# Revit family: Qmax 900
name_source: partatom
category: Plumbing Fixtures
revit_build: Autodesk Revit 2013 (Build: 20120221_2030(x64)
units: mm (PartAtom-declared; Revit-internal decimal feet)

## types (5) — shared parameters
700-900 Step Connector - Colour = Black
700-900 Step Connector - Dimensions = 860mm x 45mm x 1065mm (LxWxH)
700-900 Step Connector - Material = High Density Polyethylene
700-900 Step Connector - Model Description = High capacity slot drainage channel system
700-900 Step Connector - Product Code = 32883
700-900 Step Connector - Recyclable = Fully recyclable
700-900 Step Connector - Recycled Material Content = 0%
700-900 Step Connector - Weight = 3.7 kg
ACO Hydraulic Design Software = http://www.acodesign.co.uk
Assembly Code = D2040
Chamber Connector - Channel Colour = Black
Chamber Connector - Channel Material = Medium Density Polyethylene
Chamber Connector - Dimensions = Female End=800mm x 900mm x 1105mm, Male End=800mm x 900mm x 1055mm  (LxWXH)
Chamber Connector - Model Description = High capacity slot drainage channel system
Chamber Connector - Product Code = 32846
Chamber Connector - Recyclable = Fully recyclable
Chamber Connector - Recycled Material Content = Variable %
Chamber Connector - Weight = 25.1 kg
Channel C.S.A = 413471mm²
Channel Colour = Black
Channel Material = Medium Density Polyethylene
Channel Recyclable = Fully recyclable
Channel Recycled Material Content = Variable %
Closing End Cap - Colour = Black
Closing End Cap - Dimensions = 860mm x 16mm x 1065mm (LxWxH)
Closing End Cap - Model Description = High capacity slot drainage channel system
Closing End Cap - Product Code = 32845
Closing End Cap - Recyclable = Fully recyclable
Closing End Cap - Recycled Material Content = 0%
Closing End Cap - Weight = 9.8 kg
Concrete Surround Volume - Load Class A 15 - F 900 = 0.91 m³/m
Edge Rail Recyclable = Fully recyclable
Edge Rail Recycled Material Content = Between 40% - 90%
Fax = +44 (0)1462 815895
Hydraulic Performance = http://www.aco.co.uk
Installation - Concrete Grade = Refer to brochure
Installation - Reinforcement Details = Refer to brochure
Installation Guidelines = http://www.aco.co.uk
Length = 2000 mm  [stored 6.56168 ft]
Load Class = A 15 - F 900
Maintenance Guidelines = http://www.aco.co.uk
Manufacturer = ACO Technologies plc - ACO Water Management Division
Model = ACO Qmax 900
Model Description = High capacity slot drainage channel system
Price = POA - contact ACO
Product Brochure = http://www.aco.co.uk
Product Page URL = http://www.aco.co.uk
Product Standard = BS EN 1433:2002 CE  marked
Revision = 1
Seal Colour = Black
Seal Material = EPDM
Seal Recyclable = Fully recyclable
Seal Recycled Material Content = 0%
Telephone = +44 (0)1462 816666
URL = www.aco.co.uk
Width Overall = 860 mm
zero-valued in all types: Cost, SerialNumber, TagNumber

## per-type parameters (varying)
| type | Closing End Cap - Material | Coarse Origin | Depth Overall | Drainage Slot Intake Area | Drainage Slot Width | E1-QFlow-DuctileIron | E2-QGuard-DuctileIron | E3-QFlow-GalvSteel | E4-QGuard-GalvSteel | E5-QSlot-GalvSteel | Edge Rail Colour | Edge Rail Finish | Edge Rail Material | Endcap_Origin | Floor Opening Width | Invert Depth | Material | Product Code | Product Dimensions | Product Weight | Step Con Origin | Type Comments | V_CoarseE1 | V_Coarse_E5 |
| 32840 - Q-Flow Edge - D.I | High Density Polyethylene | 746 mm | 1270 mm | 18775mm²/m | 26mm | Yes | No | No | No | No | Black | ATec coating | Ductile Iron | 706 mm | 65 mm  [stored 0.213255 ft] | 1155mm | Iron, Ductile | 32840 | 2000mm x 860mm x 1270mm (LxWxH) | 65.3 kg | 681 mm  [stored 2.23425 ft] | ACO Qmax 900 channel assembly complete with ACO Q-Flow ductile iron edge rail | Yes | No |
| 32841 - Q-Guard Edge - D.I | High Density Polyethylene | 746 mm | 1270 mm | 10925mm²/m | 8mm twin slot | No | Yes | No | No | No | Black | ATec coating | Ductile Iron | 706 mm | 65 mm  [stored 0.213255 ft] | 1155mm | Iron, Ductile | 32841 | 2000mm x 860mm x 1270mm (LxWxH) | 66.3 kg | 681 mm  [stored 2.23425 ft] | ACO Qmax 900 channel assembly complete with ACO Q-Guard ductile iron edge rail | Yes | No |
| 32842 - Q-Flow Edge - G.S | High Density Polyethylene | 746 mm | 1270 mm | 18106mm²/m | 26mm | No | No | Yes | No | No | Silver
Silver | Galvanised | Steel | 706 mm | 90 mm  [stored 0.295276 ft] | 1155mm | Steel, Galvanized | 32842 | 2000mm x 860mm x 1270mm (LxWxH) | 57.2 kg | 681 mm  [stored 2.23425 ft] | ACO Qmax 900 channel assembly complete with ACO Q-Flow galvanised steel edge rail | Yes | No |
| 32843 - Q-Guard Edge - G.S | High Density Polyethylene | 746 mm | 1270 mm | 8356mm²/m | 10mm | No | No | No | Yes | No | Silver | Galvanised | Steel | 706 mm | 55 mm  [stored 0.180446 ft] | 1155mm | Steel, Galvanized | 32843 | 2000mm x 860mm x 1270mm (LxWxH) | 54.7 kg | 681 mm  [stored 2.23425 ft] | ACO Qmax 900 channel assembly complete with ACO Q-Guard galvanised steel edge rail | Yes | No |
| 32844 - Q-Slot Edge - G.S | High Density Polyethylene
High Density Polyethylene | 846 mm | 1370 mm | 10000mm²/m | 10mm | No | No | No | No | Yes | Silver | Galvanised | Steel | 806 mm | 18 mm  [stored 0.0590551 ft] | 1255mm | Steel, Galvanized | 32844 | 2000mm x 860mm x 1370mm (LxWxH) | 62.3 kg | 781 mm | ACO Qmax 900 channel assembly complete with ACO Q-Slot galvanised steel edge rail | No | Yes |

note: [stored X ft] marks values corroborated as IEEE doubles in the binary element streams (Revit-internal decimal feet)

## geometry (parser evidence)
native form markers: Blend x4, Sweep x14
no freeform markers — native parametric forms only
